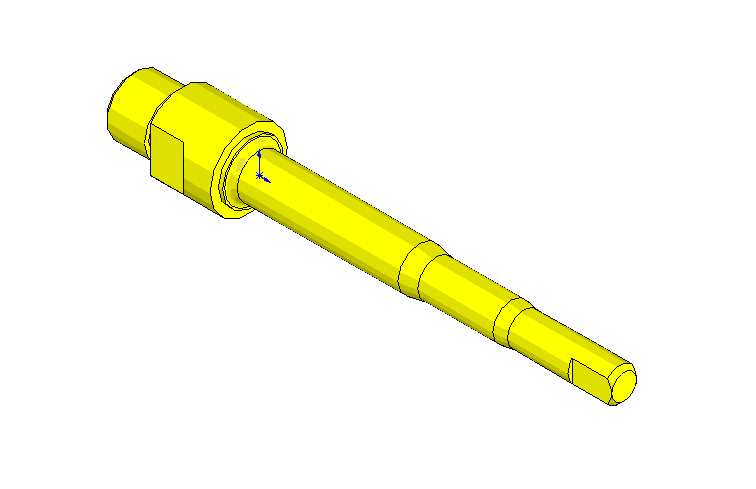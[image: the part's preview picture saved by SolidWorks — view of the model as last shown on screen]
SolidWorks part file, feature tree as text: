
SOLIDWORKS PART (.sldprt)
format: sldprt  version: not decoded by parser v0  size: 241,152 bytes
history: native  units: mm
features: plane x3, sketch x3, cut_extrude x2, material x1, revolve x1, chamfer x1 (+10 scaffold rows collapsed)
feature tree (21):
  scaffold x10  (default folders/planes/origin — collapsed)
  material  "Matériau <non spécifié>"
  plane  "Plan de face"
  plane  "Plan de dessus"
  plane  "Plan de droite"
  sketch  "Esquisse1"  dims[c1.D1=1.5mm c1.D2=12.0mm c1.D3=10.0mm c1.D4=14.0mm c1.D5=12.0mm c1.D6=16.0mm c1.D7=17.0mm c1.D8=18.5mm c1.D9=10.5mm c1.D10=14.5mm c1.D11=9.0mm c1.D12=90.0mm c1.D13=41.0mm c1.D14=45.0mm c1.D15=63.0mm c1.D16=66.0mm c1.D17=8.0mm c2.D9=13.5mm]
  revolve  "Révolution1"  Angle=360deg
  chamfer  "Chanfrein1"  Distance=1mm Angle=45deg
  sketch  "Esquisse2"  dims[D1=80.5mm D2=6.0mm]
  cut_extrude  "Enlèv. mat.-Extru.1"  [1 undecoded]
  sketch  "Esquisse4"  dims[c1.D1=15.0mm c1.D2=8.0mm c1.D3=~13.216193mm c2.D3=45.0deg]
  cut_extrude  "Enlèv. mat.-Extru.3"  [1 undecoded]
decode coverage: 5 of 7 modeling features carry decoded parameters
note: ~ marks probable driven/reference dimensions
note: 2 parameter values undecoded
note: suppression state not decoded; provenance and decode notes live in map.json
